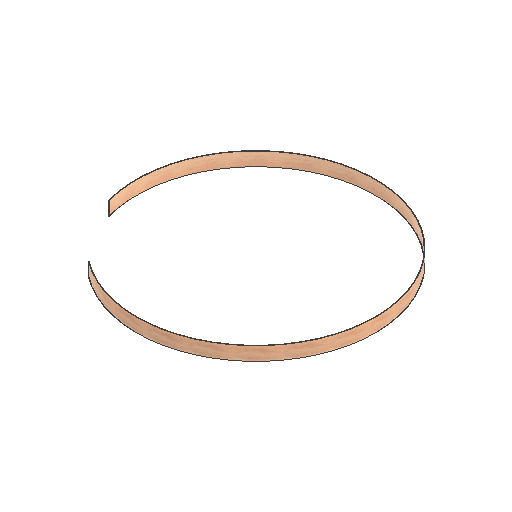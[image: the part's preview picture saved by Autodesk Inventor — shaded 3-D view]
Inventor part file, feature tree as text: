
AUTODESK INVENTOR PART (.ipt)
format: ipt  version: 2021 (Build 250183000, 183)  size: 122,880 bytes
history: native  units: mm
features: other x4, extrude x2, sketch x2, reference x2
ambient origin geometry x8: Origin, YZ Plane, XZ Plane, XY Plane, X Axis, Y Axis, Z Axis, Center Point
bodies: Solid1 (feature_tree)
feature tree (10):
  extrude  "Extrusion1"  Depth=1753.52mm
  extrude  "Extrusion2"  Depth=100.0mm TaperAngle=0.0deg
  sketch  "Sketch1"  dims[d0=1761.52mm d1=1753.52mm]
  sketch  "Sketch2"  dims[d2=100.0mm d3=0.0mm d4=100.0mm d5=0.0mm]
  reference  "Reference1"
  reference  "Reference2"
  other  "Full Scale Assembly.iam"
  other  "Disc C Assembly:1"
  other  "Platform C4:1"
  other  "Platform C1:1"
